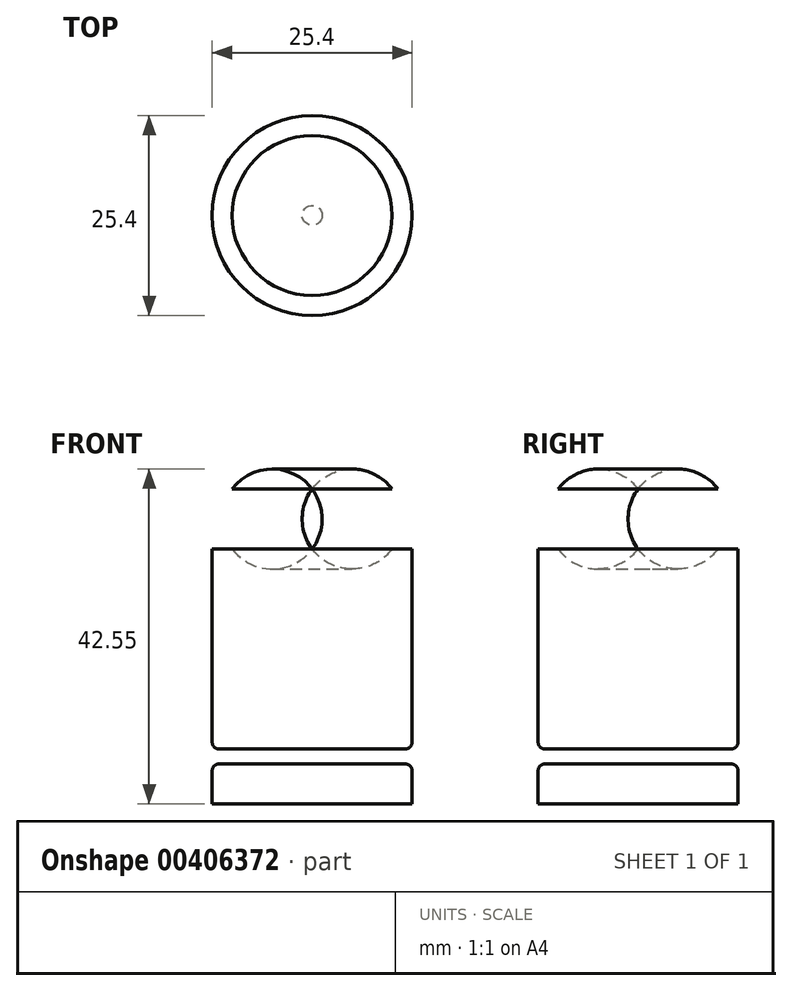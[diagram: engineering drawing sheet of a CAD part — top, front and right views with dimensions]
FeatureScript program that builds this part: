
annotation { "Feature Type Name" : "Feature", "Feature Type Description" : "" }
export const myFeature = defineFeature(function(context is Context, id is Id, definition is map)
    precondition{}
    {
        {
            var Q0;
            Q0=qCreatedBy(makeId("Front.planeOp"),FACE);
            var sketch = newSketch(context, id + "F0", { "sketchPlane" : qUnion([Q0])});
            skLineSegment(sketch, "E0.bottom", {"start": v(0, 0) * mm, "end": v(12.7, 0) * mm});
            skLineSegment(sketch, "E0.top", {"start": v(0, 5.08) * mm, "end": v(12.7, 5.08) * mm});
            skLineSegment(sketch, "E0.left", {"start": v(0, 0) * mm, "end": v(0, 5.08) * mm});
            skLineSegment(sketch, "E0.right", {"start": v(12.7, 0) * mm, "end": v(12.7, 5.08) * mm});
            skLineSegment(sketch, "E1.bottom", {"start": v(0, 5.08) * mm, "end": v(10.16, 5.08) * mm});
            skLineSegment(sketch, "E1.top", {"start": v(0, 6.99) * mm, "end": v(10.16, 6.99) * mm});
            skLineSegment(sketch, "E1.left", {"start": v(0, 5.08) * mm, "end": v(0, 6.99) * mm});
            skLineSegment(sketch, "E1.right", {"start": v(10.16, 5.08) * mm, "end": v(10.16, 6.99) * mm});
            skLineSegment(sketch, "E2.bottom", {"start": v(0, 6.99) * mm, "end": v(12.7, 6.99) * mm});
            skLineSegment(sketch, "E2.top", {"start": v(0, 32.39) * mm, "end": v(12.7, 32.39) * mm});
            skLineSegment(sketch, "E2.left", {"start": v(0, 6.99) * mm, "end": v(0, 32.39) * mm});
            skLineSegment(sketch, "E2.right", {"start": v(12.7, 6.99) * mm, "end": v(12.7, 32.39) * mm});
            skArc(sketch, "E3", {"start": v(10.16, 32.39) * mm, "mid": v(11.43, 36.2) * mm, "end": v(10.16, 40) * mm});
            skLineSegment(sketch, "E4", {"start": v(10.16, 40) * mm, "end": v(0, 40) * mm});
            skLineSegment(sketch, "E5", {"start": v(0, 32.39) * mm, "end": v(0, 40) * mm});
            skSolve(sketch);
        }
        {
            var Q0;
            {var subQ2=sQuery(id+"F0.wireOp",EDGE,"E3");Q0=makeQuery(id+"F0.imprint","IMPRINT",FACE,{"disambiguationData":[TD([[makeQuery(id+"F0.imprint","IMPRINT",EDGE,{"derivedFrom":subQ2}),1.0]])]});}
            var Q1;
            {var subQ3=sQuery(id+"F0.wireOp",EDGE,"E2.left");Q1=makeQuery(id+"F0.imprint","IMPRINT",FACE,{"disambiguationData":[TD([[makeQuery(id+"F0.imprint","IMPRINT",EDGE,{"derivedFrom":subQ3}),-1.0]])]});}
            var Q2;
            Q2=makeQuery(id+"F0.imprint","IMPRINT",FACE,{"disambiguationData":[TD([[makeQuery(id+"F0.imprint","IMPRINT",EDGE,{"derivedFrom":sQuery(id+"F0.wireOp",EDGE,"E1.bottom")}),1.0]])]});
            var Q3;
            Q3=makeQuery(id+"F0.imprint","IMPRINT",FACE,{"disambiguationData":[TD([[makeQuery(id+"F0.imprint","IMPRINT",EDGE,{"derivedFrom":sQuery(id+"F0.wireOp",EDGE,"E0.bottom")}),1.0]])]});
            var Q4;
            Q4=sQuery(id+"F0.wireOp",EDGE,"E2.left");
            revolve(context, id + "F1", {"entities" : qUnion([Q0, Q1, Q2, Q3]), "axis" : qUnion([Q4]), "revolveType" : RevolveType.FULL});
        }
        {
            var Q0;
            Q0=makeQuery(id+"F1.opRevolve","SWEPT_EDGE",EDGE,{"disambiguationData":[OSD([sQuery(id+"F0.wireOp",EDGE,"E1.right"),sQuery(id+"F0.wireOp",EDGE,"E2.bottom")])]});
            var Q1;
            Q1=makeQuery(id+"F1.opRevolve","SWEPT_EDGE",EDGE,{"disambiguationData":[OSD([sQuery(id+"F0.wireOp",EDGE,"E0.top"),sQuery(id+"F0.wireOp",EDGE,"E1.bottom"),sQuery(id+"F0.wireOp",EDGE,"E1.right")])]});
            fillet(context, id + "F2", {"entities" : qUnion([Q0, Q1]), "radius" : 0.86 * mm, "tangentPropagation" : true, "allowEdgeOverflow" : false});
        }
    });
